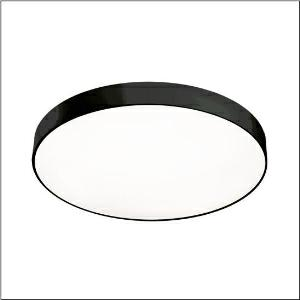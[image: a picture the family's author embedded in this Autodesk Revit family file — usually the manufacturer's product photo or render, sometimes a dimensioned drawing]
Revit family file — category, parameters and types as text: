
# Revit family: round_21_l_51mr38fd0321b
name_source: partatom
category: Lighting Fixtures
units: mm (PartAtom-declared; Revit-internal decimal feet)

## family parameters
Cut with Voids When Loaded = No
Host = Face
Light Source = No
Part Type = Normal
Room Calculation Point = No
Round Connector Dimension = Use Diameter
Shared = No

## types (1)
- Round 21 L (1 x LED, 12490 lm, 98.3 W, 3000K)
    Apparent Load = 98 VA
    CIE Flux Codes = 49 80 96 100 100
    Color Rendering = 80
    Color Temperature = 3000K
    Default Elevation = 1800 mm
    Description = Round 21 L, wall and ceiling luminaire, primary optical cover: cover, of PMMA, opal, light emission: direct distribution, primary light characteristic: symmetric, installation type: suspended mounting, surface-mounted, LED, rated luminous flux: 12.490lm, luminous efficacy: 127lm/W, light colour: 830, colour temperature: 3000K, with terminal, 5-pole, mains connection: 230V, AC, 50/60Hz, rated input power: 98W, housing, of aluminium, coated, black, diameter: 850mm, height: 62mm, protection rating (complete): IP40, insulation class (complete): insulation class I (protective earthing), certification: CE, impact resistance: IK04, permissible operating ambient temperature: -10..+35°C, packaging unit: 1 piece
    Height = 87 mm
    Lamp = 1 x LED
    Lamp Light Flux = 12490 lm
    Lamp Power = 98.3 W
    Lamp count = 1
    Length = 850 mm
    Luminous efficacy = 127 lm/W
    Manufacturer = Siteco
    ModVariant = No
    Model = 51MR38FD0321B
    Mounting Place = Ceiling
    Mounting Type = Surface mounted
    Number of Poles = 1
    OnlyDefault = Yes
    Power Factor = 1
    Product Name = Round 21 L
    Product group = wall and ceiling luminaire
    ProductGroupID = 302
    Protection Class = Protection class I
    Protection Degree = IP 40
    RLX_Detail_Level = 1
    RLX_Emergency_Light_Flux = 0 lm
    RLX_Emergency_Type = 0
    RLX_Emergency_Type_DB = No
    RlxData = <blob elided: 23873 chars, md5=c59b6852>
    Socket = socket
    Standby Power = 0 W
    System Light Flux = 12490 lm
    System Power = 98 W
    Type Comments = Product without accessories
    Type Image = l_1258328.jpg
    URL = http://relux.com
    VarID = ---
    Voltage = 0 V
    Weight = 0.00 kg
    Width = 0 mm  [stored 0 ft]

note: [stored X ft] marks values corroborated as IEEE doubles in the binary element streams (Revit-internal decimal feet)

## geometry (parser evidence)
native form markers: Blend x4, Sweep x11
no freeform markers — native parametric forms only
